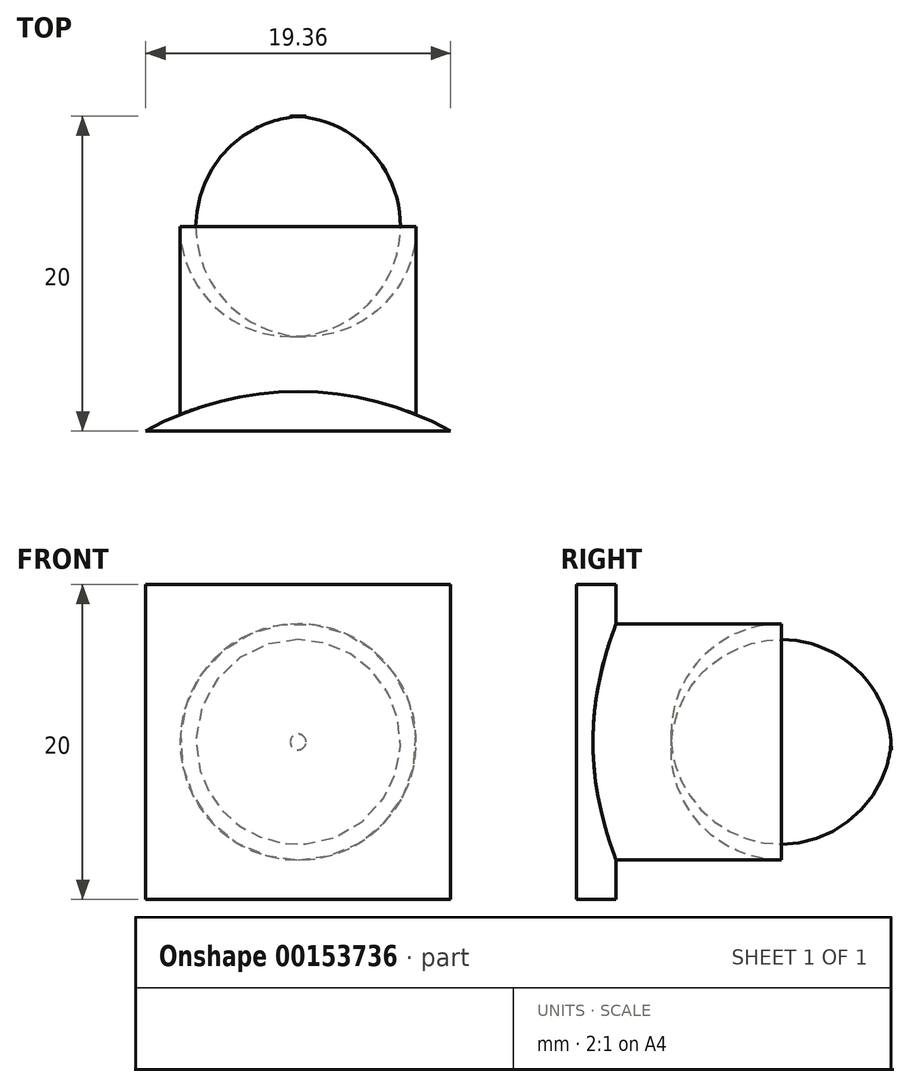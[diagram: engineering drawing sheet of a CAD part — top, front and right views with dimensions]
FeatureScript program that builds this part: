
annotation { "Feature Type Name" : "Feature", "Feature Type Description" : "" }
export const myFeature = defineFeature(function(context is Context, id is Id, definition is map)
    precondition{}
    {
        {
            var Q0;
            Q0=qCreatedBy(makeId("Top.planeOp"),FACE);
            var sketch = newSketch(context, id + "F0", { "sketchPlane" : qUnion([Q0])});
            skCircle(sketch, "E0", {"center": v(0, 0) * mm, "radius": 20 * mm, "construction": true});
            skLineSegment(sketch, "E1", {"start": v(-9.68, 17.5) * mm, "end": v(9.68, 17.5) * mm});
            skArc(sketch, "E2", {"start": v(9.68, 17.5) * mm, "mid": v(0, 20) * mm, "end": v(-9.68, 17.5) * mm});
            skSolve(sketch);
        }
        {
            var Q0;
            Q0 = qSketchRegion(id + "F0", true);
            extrude(context, id + "F1", {"entities" : qUnion([Q0]), "depth" : 20 * mm});
        }
        {
            var Q0;
            Q0=makeQuery(id+"F1.opExtrude","SWEPT_FACE",FACE,{"disambiguationData":[OSD([sQuery(id+"F0.wireOp",EDGE,"E1")])]});
            var sketch = newSketch(context, id + "F2", { "sketchPlane" : qUnion([Q0])});
            skCircle(sketch, "E3", {"center": v(0, 10) * mm, "radius": 7.5 * mm});
            skPoint(sketch, "E4", {"position": v(0, 20) * mm});
            skPoint(sketch, "E5", {"position": v(-9.68, 10) * mm});
            skSolve(sketch);
        }
        {
            var Q0;
            Q0 = qSketchRegion(id + "F2", true);
            extrude(context, id + "F3", {"entities" : qUnion([Q0]), "operationType" : NewBodyOperationType.ADD, "oppositeDirection" : true, "depth" : 20 * mm});
        }
        {
            var Q0;
            Q0=makeQuery(id+"F3.opExtrude","CAP_EDGE",EDGE,{"disambiguationData":[OSD([sQuery(id+"F2.wireOp",EDGE,"E3")])],"isStart":false});
            fillet(context, id + "F4", {"entities" : qUnion([Q0]), "radius" : 7 * mm, "tangentPropagation" : true, "allowEdgeOverflow" : false});
        }
    });
